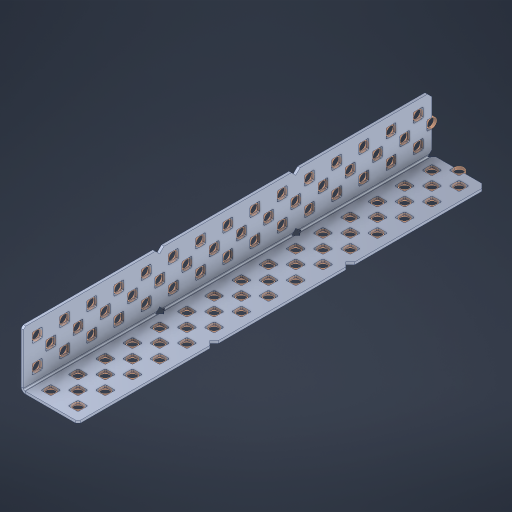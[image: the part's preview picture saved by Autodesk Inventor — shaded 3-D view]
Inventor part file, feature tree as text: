
AUTODESK INVENTOR PART (.ipt)
format: ipt  version: 2023 (Build 270158000, 158)  size: 1,224,704 bytes
history: native  units: in
note: dims shown in document units (in); Inventor stores cm internally (conversion verified against a paired STEP export)
features: other x96, extrude x88, sheet_metal_op x8, sketch x7, pattern_linear x2, mirror x1, chamfer x1
ambient origin geometry x8: Origin, YZ Plane, XZ Plane, XY Plane, X Axis, Y Axis, Z Axis, Center Point
bodies: Solid1 (feature_tree), Body (feature_tree)
feature tree (203):
  sheet_metal_op  "Flanges"
  sheet_metal_op  "Body Pattern"
  pattern_linear  "Center Pattern"  Spacing1=1.0in  [1 undecoded]
  other  "Arc Length"
  pattern_linear  "Notch Pattern"  Spacing1=0.1875in  [1 undecoded]
  other  "Diagonal Plane"
  mirror  "Everything Mirrored"
  chamfer  "End Chamfer"
  sketch  "Sketch1"  dims[d0=1.0in]
  other  "Plate1"
  sketch  "Sketch2"  dims[d1=7.5in]
  other  "Plate2"
  sheet_metal_op  "Bend1"
  sheet_metal_op  "Corner1"
  sketch  "Sketch8"  dims[d2=0.0469in]
  sketch  "Sketch9"  dims[d3=0.0469in]
  other  "Srf91"
  sheet_metal_op  "Body Pattern Sketch"
  other  "Srf92"
  sketch  "Sketch13"  dims[d4=0.0234in]
  sketch  "Sketch15"  dims[d5=0.0938in]
  sketch  "Sketch16"  dims[d6=0.0469in d7=1.0in d8=90.0deg d9=0.0312in d10=0.1875in d11=0.0469in d12=0.0469in d49=0.182in d50=0.02in d52=0.25in d53=0.0469in d54=0.0in d55=0.172in d56=1.0in d57=0.0in d60=5.9055in d62=0.5in d63=0.7874in d65=0.5in d85=0.1473in d86=0.1659in d89=0.0469in d90=0.0in d91=0.04in d92=0.0491in d95=2.5in d96=0.04in d97=0.25in d98=45.0deg d99=0.25in d106=0.182in d107=0.02in d108=0.5in d110=0.0469in d111=0.0in d112=0.172in d113=0.5in d114=0.0in d117=0.5in d123=0.25in d125=0.25in d126=0.0491in d127=0.1227in d128=0.08in d129=0.04in d130=2.5in]
  other  "Srf786"
  other  "Srf856"
  other  "Srf857"
  other  "Srf858"
  other  "Srf859"
  other  "Srf860"
  other  "Srf861"
  other  "Srf889"
  other  "Srf890"
  other  "Srf891"
  other  "Srf1275"
  other  "Srf1276"
  other  "Srf1278"
  other  "Srf1279"
  other  "Srf1280"
  other  "Srf1281"
  other  "Srf1282"
  other  "Srf1283"
  other  "Srf1277"
  other  "Srf1285"
  other  "Srf1286"
  other  "Srf1287"
  other  "Srf1383"
  other  "Srf1384"
  other  "Srf1385"
  other  "Srf1386"
  other  "Srf1387"
  other  "Srf1388"
  other  "Srf1389"
  other  "Srf1390"
  other  "Srf1391"
  other  "Srf1392"
  other  "Srf1393"
  other  "Srf1394"
  other  "Srf1395"
  other  "Srf1396"
  other  "Srf1397"
  other  "Srf1398"
  other  "Srf1399"
  other  "Srf1400"
  other  "Srf1401"
  other  "Srf1402"
  other  "Srf1403"
  other  "Srf1404"
  other  "Srf1445"
  other  "Srf1446"
  other  "Srf1447"
  other  "Srf1448"
  other  "Srf1449"
  other  "Srf1450"
  other  "Srf1451"
  other  "Srf1452"
  other  "Srf1453"
  other  "Srf1454"
  other  "Srf1455"
  other  "Srf1475"
  other  "Srf1476"
  other  "Srf1477"
  other  "Srf1478"
  other  "Srf1479"
  other  "Srf1480"
  other  "Srf1481"
  other  "Srf1482"
  other  "Srf1483"
  other  "Srf1484"
  other  "Srf1485"
  other  "Srf1486"
  other  "Srf1487"
  other  "Srf1488"
  other  "Srf1489"
  other  "Srf1490"
  other  "Srf1491"
  other  "Srf1492"
  other  "Srf1493"
  other  "Srf1494"
  other  "Srf1495"
  other  "Srf1496"
  other  "Srf1537"
  other  "Srf1538"
  other  "Srf1539"
  other  "Srf1540"
  other  "Srf1541"
  other  "Srf1542"
  other  "Srf1543"
  other  "Srf1544"
  other  "Srf1545"
  other  "Srf1546"
  other  "Srf1547"
  sheet_metal_op  "Body Stamp"
  sheet_metal_op  "Body Circle"
  other  "Center Stamp"
  other  "Center Circle"
  sheet_metal_op  "Notch"
  extrude  "ExtrusionSrf92"  Depth=0.0469in
  extrude  "ExtrusionSrf856"  Depth=0.0469in
  extrude  "ExtrusionSrf857"  Depth=2.5in
  extrude  "ExtrusionSrf858"  Depth=0.02in
  extrude  "ExtrusionSrf859"  Depth=2.5in
  extrude  "ExtrusionSrf860"  Depth=0.0469in
  extrude  "ExtrusionSrf861"  TaperAngle=0.0deg  [1 undecoded]
  extrude  "ExtrusionSrf889"  Depth=2.5in
  extrude  "ExtrusionSrf890"  Depth=1.0in TaperAngle=0.0deg
  extrude  "ExtrusionSrf891"  Depth=2.5in
  extrude  "ExtrusionSrf1275"  Depth=0.5in
  extrude  "ExtrusionSrf1276"  Depth=2.5in
  extrude  "ExtrusionSrf1277"  Depth=2.5in
  extrude  "ExtrusionSrf1278"  Depth=0.0469in
  extrude  "ExtrusionSrf1279"  Depth=2.5in TaperAngle=0.0deg
  extrude  "ExtrusionSrf1280"  Depth=2.5in
  extrude  "ExtrusionSrf1281"  Depth=2.5in TaperAngle=45.0deg
  extrude  "ExtrusionSrf1282"  Depth=2.5in
  extrude  "ExtrusionSrf1345"  Depth=2.5in
  extrude  "ExtrusionSrf1346"  Depth=0.02in
  extrude  "ExtrusionSrf1347"  Depth=0.5in
  extrude  "ExtrusionSrf1348"  Depth=0.0469in
  extrude  "ExtrusionSrf1383"  TaperAngle=0.0deg  [1 undecoded]
  extrude  "ExtrusionSrf1384"  Depth=2.5in
  extrude  "ExtrusionSrf1385"  Depth=0.5in TaperAngle=0.0deg
  extrude  "ExtrusionSrf1386"  Depth=0.5in
  extrude  "ExtrusionSrf1387"  Depth=2.5in
  extrude  "ExtrusionSrf1388"  Depth=2.5in
  extrude  "ExtrusionSrf1389"  Depth=2.5in
  extrude  "ExtrusionSrf1390"  Depth=2.5in
  extrude  "ExtrusionSrf1391"  Depth=2.5in
  extrude  "ExtrusionSrf1392"  Depth=2.5in
  extrude  "ExtrusionSrf1393"  Depth=2.5in
  extrude  "ExtrusionSrf1394"  [1 undecoded]
  extrude  "ExtrusionSrf1395"  [1 undecoded]
  extrude  "ExtrusionSrf1396"  [1 undecoded]
  extrude  "ExtrusionSrf1397"  [1 undecoded]
  extrude  "ExtrusionSrf1398"  [1 undecoded]
  extrude  "ExtrusionSrf1399"  [1 undecoded]
  extrude  "ExtrusionSrf1400"  [1 undecoded]
  extrude  "ExtrusionSrf1401"  [1 undecoded]
  extrude  "ExtrusionSrf1402"  [1 undecoded]
  extrude  "ExtrusionSrf1403"  [1 undecoded]
  extrude  "ExtrusionSrf1404"  [1 undecoded]
  extrude  "ExtrusionSrf1445"  [1 undecoded]
  extrude  "ExtrusionSrf1446"  [1 undecoded]
  extrude  "ExtrusionSrf1447"  [1 undecoded]
  extrude  "ExtrusionSrf1448"  [1 undecoded]
  extrude  "ExtrusionSrf1449"  [1 undecoded]
  extrude  "ExtrusionSrf1450"  [1 undecoded]
  extrude  "ExtrusionSrf1451"  [1 undecoded]
  extrude  "ExtrusionSrf1452"  [1 undecoded]
  extrude  "ExtrusionSrf1453"  [1 undecoded]
  extrude  "ExtrusionSrf1454"  [1 undecoded]
  extrude  "ExtrusionSrf1455"  [1 undecoded]
  extrude  "ExtrusionSrf1475"  [1 undecoded]
  extrude  "ExtrusionSrf1476"  [1 undecoded]
  extrude  "ExtrusionSrf1477"  [1 undecoded]
  extrude  "ExtrusionSrf1478"  [1 undecoded]
  extrude  "ExtrusionSrf1479"  [1 undecoded]
  extrude  "ExtrusionSrf1480"  [1 undecoded]
  extrude  "ExtrusionSrf1481"  [1 undecoded]
  extrude  "ExtrusionSrf1482"  [1 undecoded]
  extrude  "ExtrusionSrf1483"  [1 undecoded]
  extrude  "ExtrusionSrf1484"  [1 undecoded]
  extrude  "ExtrusionSrf1485"  [1 undecoded]
  extrude  "ExtrusionSrf1486"  [1 undecoded]
  extrude  "ExtrusionSrf1487"  [1 undecoded]
  extrude  "ExtrusionSrf1488"  [1 undecoded]
  extrude  "ExtrusionSrf1489"  [1 undecoded]
  extrude  "ExtrusionSrf1490"  [1 undecoded]
  extrude  "ExtrusionSrf1491"  [1 undecoded]
  extrude  "ExtrusionSrf1492"  [1 undecoded]
  extrude  "ExtrusionSrf1493"  [1 undecoded]
  extrude  "ExtrusionSrf1494"  [1 undecoded]
  extrude  "ExtrusionSrf1495"  [1 undecoded]
  extrude  "ExtrusionSrf1496"  [1 undecoded]
  extrude  "ExtrusionSrf1537"  [1 undecoded]
  extrude  "ExtrusionSrf1538"  [1 undecoded]
  extrude  "ExtrusionSrf1539"  [1 undecoded]
  extrude  "ExtrusionSrf1540"  [1 undecoded]
  extrude  "ExtrusionSrf1541"  [1 undecoded]
  extrude  "ExtrusionSrf1542"  [1 undecoded]
  extrude  "ExtrusionSrf1543"  [1 undecoded]
  extrude  "ExtrusionSrf1544"  [1 undecoded]
  extrude  "ExtrusionSrf1545"  [1 undecoded]
  extrude  "ExtrusionSrf1546"  [1 undecoded]
  extrude  "ExtrusionSrf1547"  [1 undecoded]
note: 59 required parameter values undecoded (feature->parameter linkage not recoverable at this tier; creation-order binding heuristic only, values carry confidence <= 0.55)
